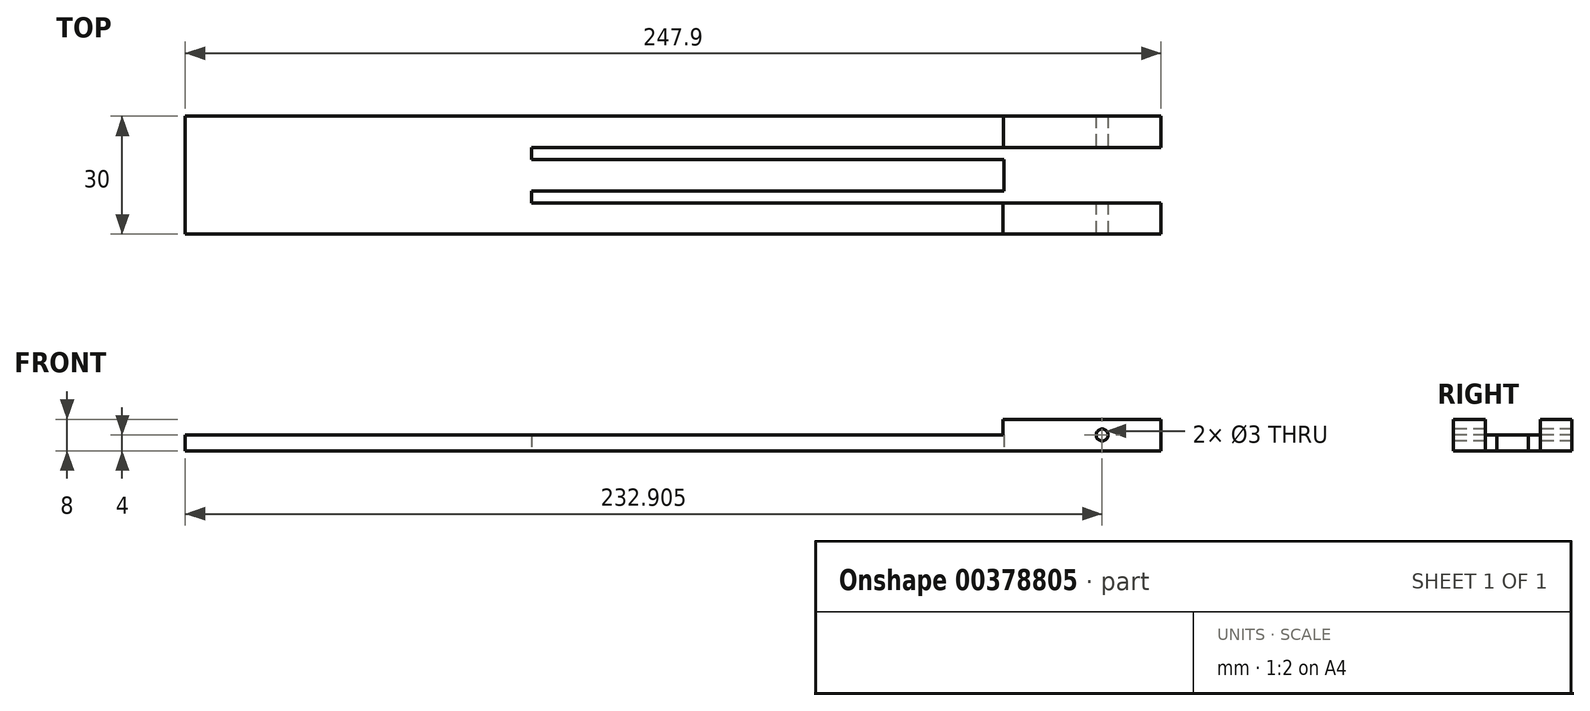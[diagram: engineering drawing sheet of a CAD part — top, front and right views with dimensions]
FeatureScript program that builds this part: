
annotation { "Feature Type Name" : "Feature", "Feature Type Description" : "" }
export const myFeature = defineFeature(function(context is Context, id is Id, definition is map)
    precondition{}
    {
        {
            var Q0;
            Q0=qCreatedBy(makeId("Top.planeOp"),FACE);
            var sketch = newSketch(context, id + "F0", { "sketchPlane" : qUnion([Q0])});
            skLineSegment(sketch, "E0.bottom", {"start": v(123.95, -15) * mm, "end": v(-123.95, -15) * mm});
            skLineSegment(sketch, "E0.left", {"start": v(123.95, -15) * mm, "end": v(123.95, -7) * mm});
            skPoint(sketch, "E0.middle", {"position": v(0, 0) * mm});
            skLineSegment(sketch, "E1.bottom", {"start": v(84.02, -4) * mm, "end": v(-36.05, -4) * mm});
            skLineSegment(sketch, "E1.top", {"start": v(123.95, -7) * mm, "end": v(-36.05, -7) * mm});
            skLineSegment(sketch, "E1.right", {"start": v(-36.05, -4) * mm, "end": v(-36.05, -7) * mm});
            skLineSegment(sketch, "E2", {"start": v(83.96, 4) * mm, "end": v(83.95, 4) * mm});
            skLineSegment(sketch, "E3.right", {"start": v(84.02, 4) * mm, "end": v(84.02, -4) * mm});
            skLineSegment(sketch, "E4", {"start": v(-123.95, 15) * mm, "end": v(-123.95, -15) * mm});
            skLineSegment(sketch, "E5", {"start": v(-123.95, 15) * mm, "end": v(123.95, 15) * mm});
            skLineSegment(sketch, "E6", {"start": v(123.95, 15) * mm, "end": v(123.95, 7) * mm});
            skLineSegment(sketch, "E7", {"start": v(-36.05, 7) * mm, "end": v(123.95, 7) * mm});
            skLineSegment(sketch, "E8", {"start": v(-36.05, 7) * mm, "end": v(-36.05, 4) * mm});
            skLineSegment(sketch, "E9", {"start": v(-36.05, 4) * mm, "end": v(84.02, 4) * mm});
            skSolve(sketch);
        }
        {
            var Q0;
            Q0=makeQuery(id+"F0.imprint","IMPRINT",FACE,{"disambiguationData":[TD([[makeQuery(id+"F0.imprint","IMPRINT",EDGE,{"derivedFrom":sQuery(id+"F0.wireOp",EDGE,"E0.bottom")}),-1.0]])]});
            extrude(context, id + "F1", {"entities" : qUnion([Q0]), "depth" : 4 * mm});
        }
        {
            var Q0;
            Q0=makeQuery(id+"F1.opExtrude","CAP_FACE",FACE,{"disambiguationData":[OSD([sQuery(id+"F0.wireOp",EDGE,"E0.bottom"),sQuery(id+"F0.wireOp",EDGE,"E0.left"),sQuery(id+"F0.wireOp",EDGE,"E1.bottom"),sQuery(id+"F0.wireOp",EDGE,"E1.top"),sQuery(id+"F0.wireOp",EDGE,"E1.right"),sQuery(id+"F0.wireOp",EDGE,"E3.right"),sQuery(id+"F0.wireOp",EDGE,"E4"),sQuery(id+"F0.wireOp",EDGE,"E5"),sQuery(id+"F0.wireOp",EDGE,"E6"),sQuery(id+"F0.wireOp",EDGE,"E7"),sQuery(id+"F0.wireOp",EDGE,"E8"),sQuery(id+"F0.wireOp",EDGE,"E9")])],"isStart":false});
            var sketch = newSketch(context, id + "F2", { "sketchPlane" : qUnion([Q0])});
            skLineSegment(sketch, "E10.bottom", {"start": v(123.95, 15) * mm, "end": v(83.96, 15) * mm});
            skLineSegment(sketch, "E10.top", {"start": v(123.95, 7) * mm, "end": v(83.96, 7) * mm});
            skLineSegment(sketch, "E10.left", {"start": v(123.95, 15) * mm, "end": v(123.95, 7) * mm});
            skLineSegment(sketch, "E10.right", {"start": v(83.96, 15) * mm, "end": v(83.96, 7) * mm});
            skLineSegment(sketch, "E11.bottom", {"start": v(123.95, -7) * mm, "end": v(83.8, -7) * mm});
            skLineSegment(sketch, "E11.top", {"start": v(123.95, -15) * mm, "end": v(83.8, -15) * mm});
            skLineSegment(sketch, "E11.left", {"start": v(123.95, -7) * mm, "end": v(123.95, -15) * mm});
            skLineSegment(sketch, "E11.right", {"start": v(83.8, -7) * mm, "end": v(83.8, -15) * mm});
            skSolve(sketch);
        }
        {
            var Q0;
            Q0=qSketchRegion(id+"F2",true);
            extrude(context, id + "F3", {"entities" : qUnion([Q0]), "operationType" : NewBodyOperationType.ADD, "depth" : 4 * mm});
        }
        {
            var Q0;
            Q0=qSketchRegion(id+"F2",true);
            extrude(context, id + "F4", {"entities" : qUnion([Q0]), "operationType" : NewBodyOperationType.ADD, "depth" : 4 * mm});
        }
        {
            var Q0;
            Q0=makeQuery(id+"F3.boolean.opBoolean","MERGE",FACE,{"derivedFrom":[makeQuery(id+"F1.opExtrude","SWEPT_FACE",FACE,{"disambiguationData":[OSD([sQuery(id+"F0.wireOp",EDGE,"E0.bottom")])]}),makeQuery(id+"F3.opExtrude","SWEPT_FACE",FACE,{"disambiguationData":[OSD([sQuery(id+"F2.wireOp",EDGE,"E11.top")])]})]});
            var sketch = newSketch(context, id + "F5", { "sketchPlane" : qUnion([Q0])});
            skCircle(sketch, "E12", {"center": v(108.95, 4) * mm, "radius": 1.5 * mm});
            skPoint(sketch, "E13.top.end.orphan", {"position": v(108.95, 0) * mm});
            skPoint(sketch, "E13.bottom.end.orphan", {"position": v(108.95, 8) * mm});
            skSolve(sketch);
        }
        {
            var Q0;
            Q0=makeQuery(id+"F5.imprint","IMPRINT",FACE,{"disambiguationData":[TD([[makeQuery(id+"F5.imprint","IMPRINT",EDGE,{"derivedFrom":sQuery(id+"F5.wireOp",EDGE,"E12")}),1.0]])]});
            extrude(context, id + "F6", {"entities" : qUnion([Q0]), "operationType" : NewBodyOperationType.REMOVE, "oppositeDirection" : true, "depth" : 43 * mm});
        }
    });
